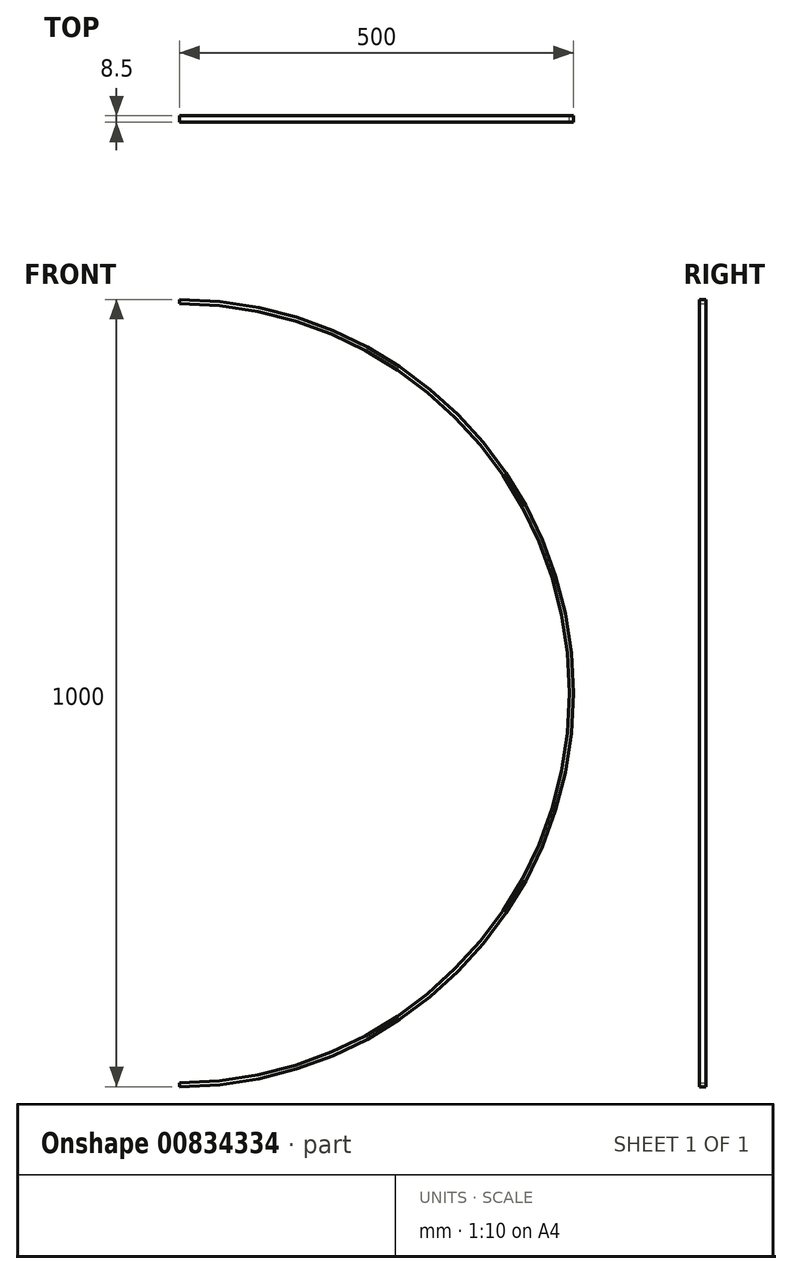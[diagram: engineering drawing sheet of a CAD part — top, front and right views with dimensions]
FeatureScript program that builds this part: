
annotation { "Feature Type Name" : "Feature", "Feature Type Description" : "" }
export const myFeature = defineFeature(function(context is Context, id is Id, definition is map)
    precondition{}
    {
        {
            var Q0;
            Q0=qCreatedBy(makeId("Front.planeOp"),FACE);
            var sketch = newSketch(context, id + "F0", { "sketchPlane" : qUnion([Q0])});
            skPoint(sketch, "E0", {"position": v(495, 0) * mm});
            skArc(sketch, "E1", {"start": v(0, -495) * mm, "mid": v(495, 0) * mm, "end": v(0, 495) * mm});
            skLineSegment(sketch, "E2", {"start": v(0, 500) * mm, "end": v(0, 495) * mm});
            skPoint(sketch, "E3", {"position": v(0, 495) * mm});
            skPoint(sketch, "E4", {"position": v(0, -495) * mm});
            skPoint(sketch, "E5", {"position": v(0, 500) * mm});
            skPoint(sketch, "E6", {"position": v(0, -500) * mm});
            skArc(sketch, "E7", {"start": v(0, -500) * mm, "mid": v(500, 0) * mm, "end": v(0, 500) * mm});
            skLineSegment(sketch, "E8.trimOffspring", {"start": v(0, -495) * mm, "end": v(0, -500) * mm});
            skSolve(sketch);
        }
        {
            var Q0;
            Q0 = qSketchRegion(id + "F0", true);
            extrude(context, id + "F1", {"entities" : qUnion([Q0]), "depth" : 8.5 * mm, "offsetDistance" : 25 * mm});
        }
    });
